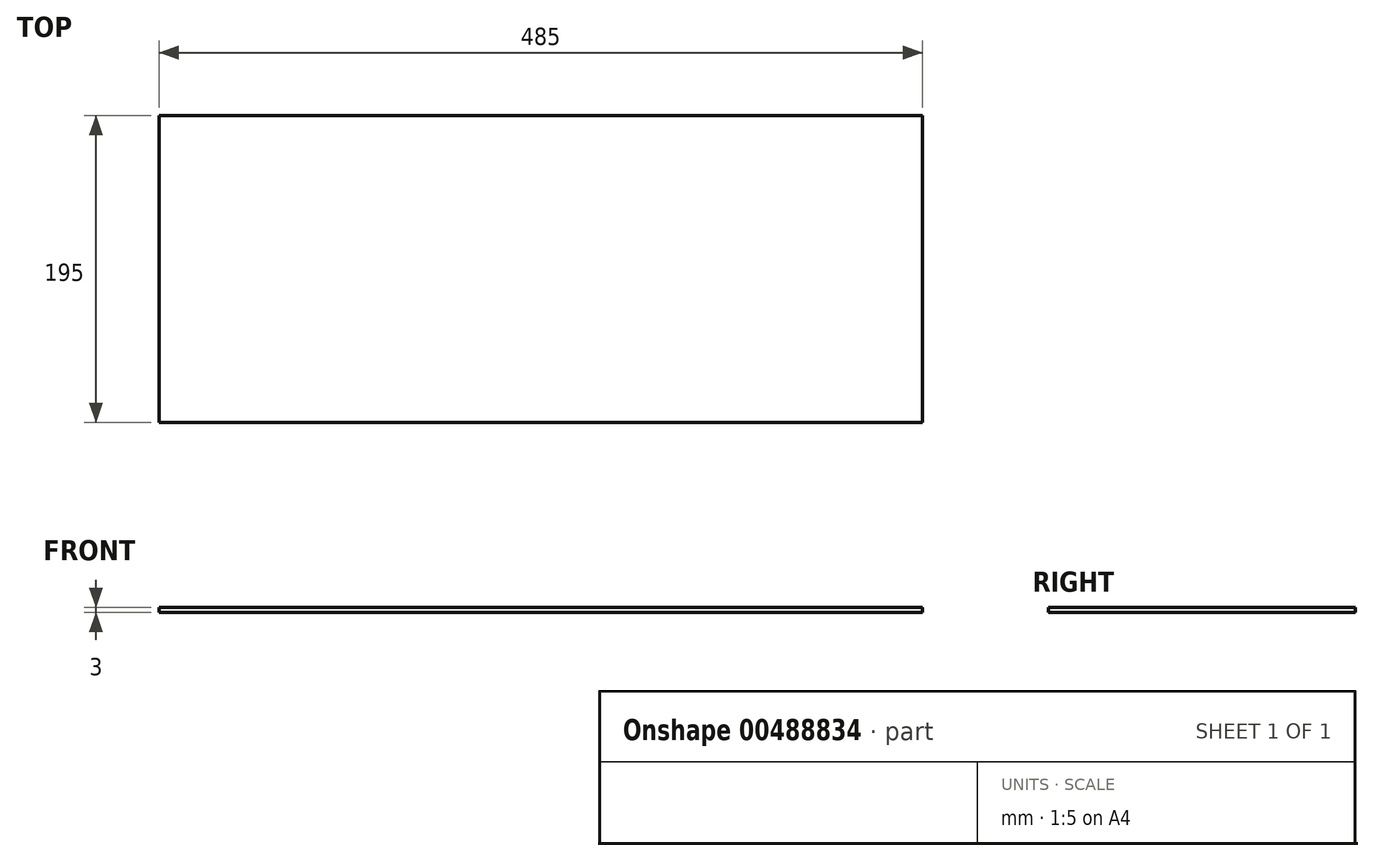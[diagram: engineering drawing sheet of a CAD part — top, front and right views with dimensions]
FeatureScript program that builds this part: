
annotation { "Feature Type Name" : "Feature", "Feature Type Description" : "" }
export const myFeature = defineFeature(function(context is Context, id is Id, definition is map)
    precondition{}
    {
        {
            var Q0;
            Q0=qCreatedBy(makeId("Top.planeOp"),FACE);
            var sketch = newSketch(context, id + "F0", { "sketchPlane" : qUnion([Q0])});
            skLineSegment(sketch, "E0.bottom", {"start": v(-240.67, 151.01) * mm, "end": v(244.33, 151.01) * mm});
            skLineSegment(sketch, "E0.top", {"start": v(-240.67, -43.99) * mm, "end": v(244.33, -43.99) * mm});
            skLineSegment(sketch, "E0.left", {"start": v(-240.67, 151.01) * mm, "end": v(-240.67, -43.99) * mm});
            skLineSegment(sketch, "E0.right", {"start": v(244.33, 151.01) * mm, "end": v(244.33, -43.99) * mm});
            skSolve(sketch);
        }
        {
            var Q0;
            Q0=makeQuery(id+"F0.imprint","IMPRINT",FACE,{"disambiguationData":[TD([[makeQuery(id+"F0.imprint","IMPRINT",EDGE,{"derivedFrom":sQuery(id+"F0.wireOp",EDGE,"E0.bottom")}),-1.0]])]});
            extrude(context, id + "F1", {"entities" : qUnion([Q0]), "depth" : 3 * mm});
        }
    });
